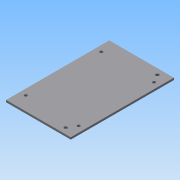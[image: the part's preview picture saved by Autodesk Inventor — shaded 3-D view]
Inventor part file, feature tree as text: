
AUTODESK INVENTOR PART (.ipt)
format: ipt  version: 2015 (Build 190159000, 159)  size: 93,696 bytes
history: native  units: in
note: dims shown in document units (in); Inventor stores cm internally (conversion verified against a paired STEP export)
features: sketch x3, hole x2, extrude x1
ambient origin geometry x8: Origin, YZ Plane, XZ Plane, XY Plane, X Axis, Y Axis, Z Axis, Center Point
bodies: Solid1 (feature_tree)
feature tree (6):
  extrude  "Extrusion1"  Depth=4.785in
  hole  "Hole1"  [1 undecoded]
  hole  "Hole2"  [1 undecoded]
  sketch  "Sketch1"  dims[d0=3.0in d1=4.785in]
  sketch  "Sketch2"  dims[d2=0.0938in d3=0.0in d4=3.5in]
  sketch  "Sketch3"  dims[d5=2.45in d6=0.136in d7=0.75in d8=0.279in d9=0.25in d10=0.5635in d11=1.0in d12=0.8108in d13=0.5in d14=4.25in d15=0.15in d16=0.75in d17=0.279in d18=0.25in d19=0.5635in d20=1.0in d21=0.8108in]
note: 2 required parameter values undecoded (feature->parameter linkage not recoverable at this tier; creation-order binding heuristic only, values carry confidence <= 0.55)
